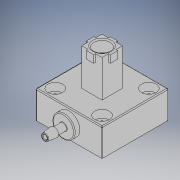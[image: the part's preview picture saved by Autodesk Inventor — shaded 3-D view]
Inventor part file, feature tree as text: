
AUTODESK INVENTOR PART (.ipt)
format: ipt  version: 2019 (Build 230136000, 136)  size: 318,976 bytes
history: native  units: mm
features: sketch x9, extrude x4, plane x3, revolve x2, fillet x2, projected_geometry x2, sweep x1, hole x1, pattern_circular x1
ambient origin geometry x8: Origin, YZ Plane, XZ Plane, XY Plane, X Axis, Y Axis, Z Axis, Center Point
bodies: Solid1 (feature_tree)
feature tree (25):
  revolve  "Revolution1"  [1 undecoded]
  plane  "Work Plane1"
  extrude  "Extrusion1"  Depth=0.35mm
  plane  "Work Plane7"
  extrude  "Extrusion6"  Depth=0.75mm
  extrude  "Extrusion7"  TaperAngle=90.0deg  [1 undecoded]
  sketch  "Sketch17"  dims[d11=0.0mm d14=2.0mm d15=0.0mm d45=0.0mm]
  plane  "Work Plane8"
  sweep  "Sweep3"
  fillet  "Fillet1"  [1 undecoded]
  hole  "Hole3"  [1 undecoded]
  revolve  "Revolution2"  [1 undecoded]
  fillet  "Fillet2"  Radius=32.7mm
  extrude  "Extrusion13"  Depth=3.0mm
  pattern_circular  "Circular Pattern1"  [2 undecoded]
  sketch  "Sketch1"  dims[d0=5.5mm d1=20.0mm]
  sketch  "Sketch2"  dims[d5=9.0mm d6=0.35mm]
  sketch  "Sketch11"  dims[d7=0.75mm d8=0.75mm]
  sketch  "Sketch16"  dims[d9=0.75mm d10=90.0deg]
  projected_geometry  "Projected Loop9"
  sketch  "Sketch18"  dims[d47=15.0mm d48=0.0mm d60=36.0mm]
  sketch  "Sketch19"  dims[d61=36.0mm d64=8.45mm d65=32.7mm d66=0.0mm]
  sketch  "Sketch21"  dims[d67=0.0mm d68=0.0mm d69=3.0mm]
  sketch  "Sketch28"  dims[d70=25.4mm d71=25.4mm d72=4.496mm d73=6.0mm d74=7.938mm d75=4.166mm d76=90.0deg d77=19.05mm d78=20.594885mm d79=3.0mm d80=6.0mm d81=5.0mm d82=1.8796mm d83=0.25mm d84=2.413mm d85=5.08mm d86=1.15mm d87=0.25mm d88=0.25mm d89=90.0deg d90=0.5mm d124=0.0mm d125=0.0mm d126=4.0mm d127=1.0mm d128=0.0mm d129=40.0mm d130=360.0deg]
  projected_geometry  "Projected Loop13"
note: 7 required parameter values undecoded (feature->parameter linkage not recoverable at this tier; creation-order binding heuristic only, values carry confidence <= 0.55)